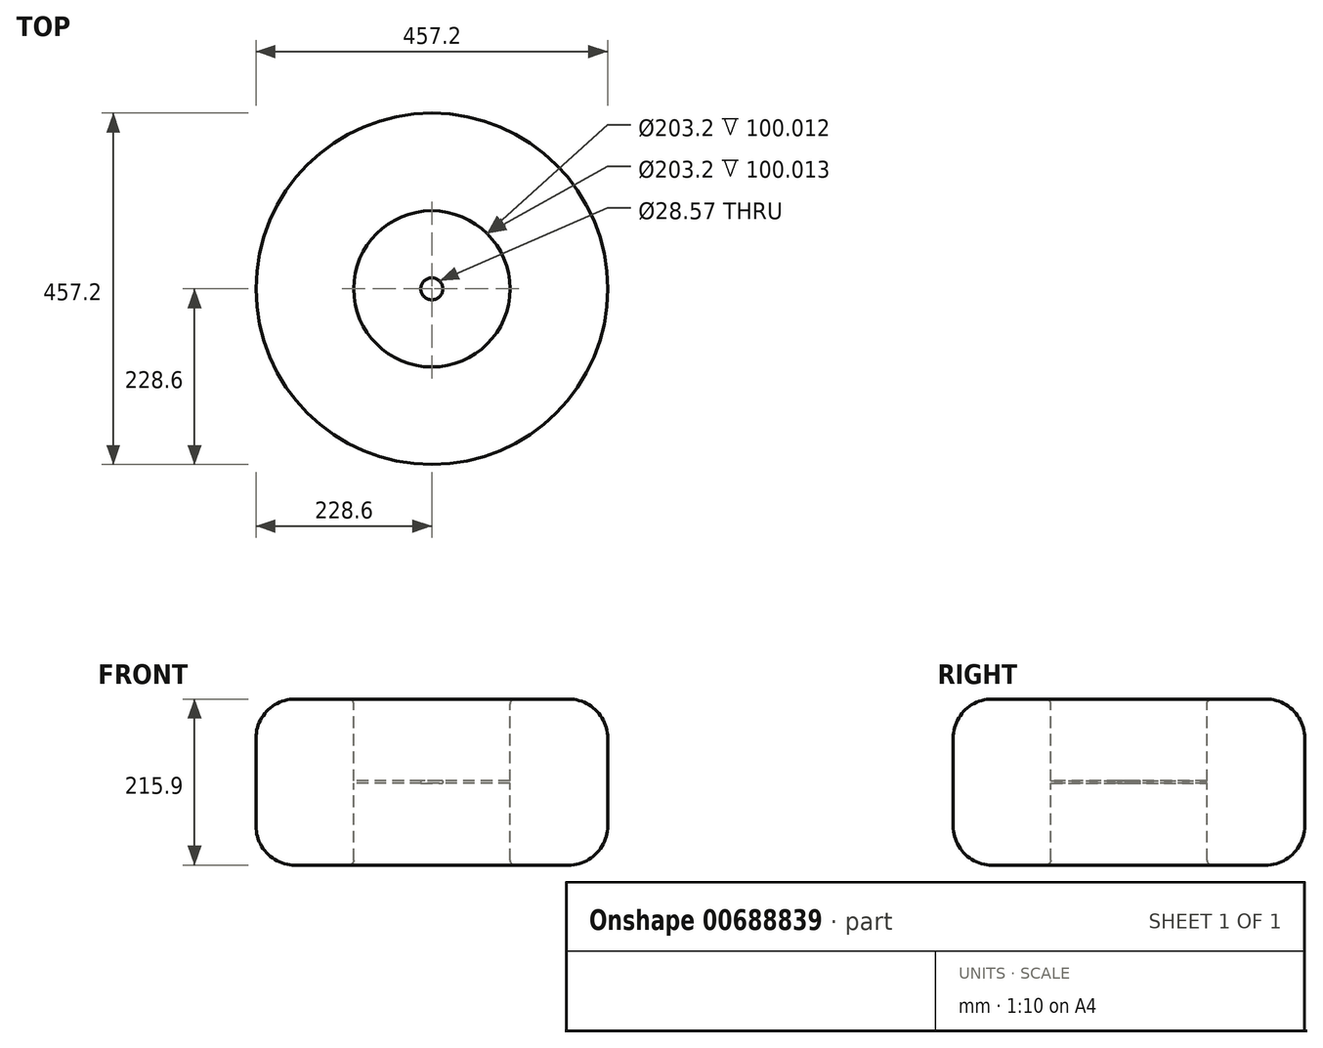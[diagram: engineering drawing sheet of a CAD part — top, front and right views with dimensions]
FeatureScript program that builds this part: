
annotation { "Feature Type Name" : "Feature", "Feature Type Description" : "" }
export const myFeature = defineFeature(function(context is Context, id is Id, definition is map)
    precondition{}
    {
        {
            var Q0;
            Q0=qCreatedBy(makeId("Right.planeOp"),FACE);
            var sketch = newSketch(context, id + "F0", { "sketchPlane" : qUnion([Q0])});
            skLineSegment(sketch, "E0.left", {"start": v(0, 106.36) * mm, "end": v(0, 109.54) * mm});
            skLineSegment(sketch, "E0.right", {"start": v(101.6, 6.35) * mm, "end": v(101.6, 109.54) * mm});
            skLineSegment(sketch, "E1", {"start": v(50.8, 107.95) * mm, "end": v(0, 107.95) * mm});
            skLineSegment(sketch, "E2.bottom", {"start": v(101.6, 107.95) * mm, "end": v(0, 107.95) * mm});
            skLineSegment(sketch, "E2.left", {"start": v(101.6, 107.95) * mm, "end": v(101.6, 107.95) * mm});
            skLineSegment(sketch, "E2.right", {"start": v(0, 107.95) * mm, "end": v(0, 107.95) * mm});
            skLineSegment(sketch, "E3.bottom", {"start": v(0, 109.54) * mm, "end": v(101.6, 109.54) * mm});
            skLineSegment(sketch, "E3.top", {"start": v(0, 106.36) * mm, "end": v(101.6, 106.36) * mm});
            skLineSegment(sketch, "E3.left", {"start": v(0, 109.54) * mm, "end": v(0, 106.36) * mm});
            skLineSegment(sketch, "E3.right", {"start": v(101.6, 109.54) * mm, "end": v(101.6, 106.36) * mm});
            skPoint(sketch, "E3.middle", {"position": v(50.8, 107.95) * mm});
            skLineSegment(sketch, "E4.bottom", {"start": v(107.95, 0) * mm, "end": v(177.8, 0) * mm});
            skLineSegment(sketch, "E4.top", {"start": v(107.95, 215.9) * mm, "end": v(177.8, 215.9) * mm});
            skLineSegment(sketch, "E4.left", {"start": v(101.6, 0) * mm, "end": v(101.6, 209.55) * mm});
            skLineSegment(sketch, "E4.right", {"start": v(228.6, 50.8) * mm, "end": v(228.6, 165.1) * mm});
            skPoint(sketch, "E5.visualSharp", {"position": v(228.6, 215.9) * mm});
            skArc(sketch, "E5.filletArc", {"start": v(228.6, 165.1) * mm, "mid": v(213.72, 201.02) * mm, "end": v(177.8, 215.9) * mm});
            skPoint(sketch, "E6.visualSharp", {"position": v(228.6, 0) * mm});
            skArc(sketch, "E6.filletArc", {"start": v(177.8, 0) * mm, "mid": v(213.72, 14.88) * mm, "end": v(228.6, 50.8) * mm});
            skPoint(sketch, "E7.orphan", {"position": v(0, 215.9) * mm});
            skPoint(sketch, "E8.orphan", {"position": v(0, 0) * mm});
            skPoint(sketch, "E9.orphan", {"position": v(101.6, 215.9) * mm});
            skArc(sketch, "E10.filletArc", {"start": v(107.95, 215.9) * mm, "mid": v(103.46, 214.04) * mm, "end": v(101.6, 209.55) * mm});
            skPoint(sketch, "E11.visualSharp", {"position": v(101.6, 0) * mm});
            skArc(sketch, "E11.filletArc", {"start": v(101.6, 6.35) * mm, "mid": v(103.46, 1.86) * mm, "end": v(107.95, 0) * mm});
            skSolve(sketch);
        }
        {
            var Q0;
            Q0=makeQuery(id+"F0.imprint","IMPRINT",FACE,{"disambiguationData":[TD([[makeQuery(id+"F0.imprint","IMPRINT",EDGE,{"derivedFrom":sQuery(id+"F0.wireOp",EDGE,"E4.bottom")}),1.0]])]});
            var Q1;
            {var subQ3=sQuery(id+"F0.wireOp",EDGE,"E2.bottom");Q1=makeQuery(id+"F0.imprint","IMPRINT",FACE,{"disambiguationData":[TD([[makeQuery(id+"F0.imprint","IMPRINT",EDGE,{"derivedFrom":subQ3}),1.0]])]});}
            var Q2;
            {var subQ3=sQuery(id+"F0.wireOp",EDGE,"E2.bottom");Q2=makeQuery(id+"F0.imprint","IMPRINT",FACE,{"disambiguationData":[TD([[makeQuery(id+"F0.imprint","IMPRINT",EDGE,{"derivedFrom":subQ3}),-1.0]])]});}
            var Q3;
            Q3=sQuery(id+"F0.wireOp",EDGE,"E3.top");
            var Q4;
            Q4=sQuery(id+"F0.wireOp",EDGE,"E4.top");
            var Q5;
            Q5=sQuery(id+"F0.wireOp",EDGE,"E10.filletArc");
            var Q6;
            Q6=sQuery(id+"F0.wireOp",EDGE,"E5.filletArc");
            var Q7;
            Q7=sQuery(id+"F0.wireOp",EDGE,"E4.right");
            var Q8;
            Q8=sQuery(id+"F0.wireOp",EDGE,"E6.filletArc");
            var Q9;
            Q9=sQuery(id+"F0.wireOp",EDGE,"E4.bottom");
            var Q10;
            Q10=sQuery(id+"F0.wireOp",EDGE,"E11.filletArc");
            var Q11;
            Q11=sQuery(id+"F0.wireOp",EDGE,"E4.left");
            var Q12;
            Q12=sQuery(id+"F0.wireOp",EDGE,"E3.bottom");
            var Q13;
            Q13=sQuery(id+"F0.wireOp",EDGE,"E3.left");
            var Q14;
            Q14=sQuery(id+"F0.wireOp",EDGE,"E3.left");
            revolve(context, id + "F1", {"entities" : qUnion([Q0, Q1, Q2]), "surfaceEntities" : qUnion([Q3, Q4, Q5, Q6, Q7, Q8, Q9, Q10, Q11, Q12, Q13]), "axis" : qUnion([Q14]), "revolveType" : RevolveType.FULL});
        }
        {
            var Q0;
            Q0=makeQuery(id+"F1.opRevolve","SWEPT_FACE",FACE,{"disambiguationData":[OSD([sQuery(id+"F0.wireOp",EDGE,"E3.top")])]});
            var sketch = newSketch(context, id + "F2", { "sketchPlane" : qUnion([Q0])});
            skCircle(sketch, "E12", {"center": v(0, 0) * mm, "radius": 14.29 * mm});
            skSolve(sketch);
        }
        {
            var Q0;
            Q0=makeQuery(id+"F2.imprint","IMPRINT",FACE,{"disambiguationData":[TD([[makeQuery(id+"F2.imprint","IMPRINT",EDGE,{"derivedFrom":sQuery(id+"F2.wireOp",EDGE,"E12")}),1.0]])]});
            extrude(context, id + "F3", {"entities" : qUnion([Q0]), "operationType" : NewBodyOperationType.REMOVE, "oppositeDirection" : true, "depth" : 25.4 * mm, "offsetDistance" : 25.4 * mm});
        }
    });
